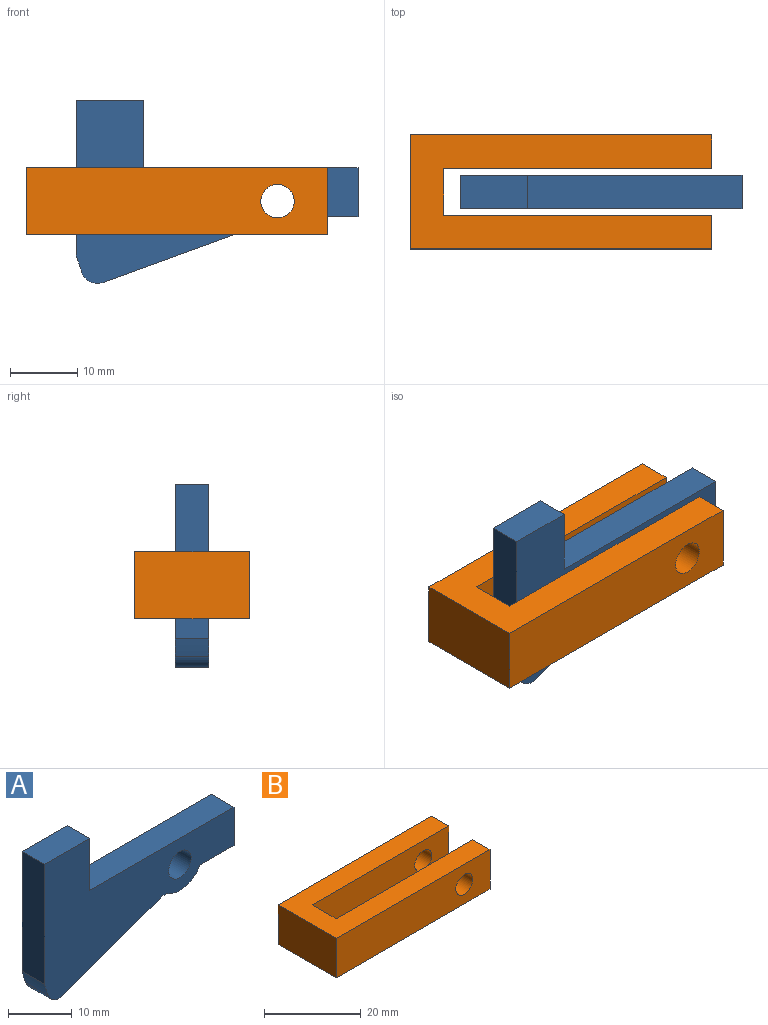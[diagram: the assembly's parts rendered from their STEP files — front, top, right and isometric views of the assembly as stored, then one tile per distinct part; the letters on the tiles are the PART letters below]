
ASSEMBLY  parts=2 mates=1
PART A: 14 faces, bbox 42x5x27.3 mm
  f0: plane 32x5mm, normal (0,0,1), area 160mm2, adj f1,f8,f10,f11
  f1: plane 10x5mm, normal (1,0,0), area 50mm2, adj f0,f2,f10,f11
  f2: plane 10x5mm, normal (0,0,1), area 50mm2, adj f1,f3,f10,f11
  f3: plane 23x5mm, normal (-1,0,0), area 115mm2, adj f2,f4,f10,f11
  f4: cylinder r=31.05mm len=5mm, axis (0,1,0), area 13.7mm2, adj f3,f10,f11,f13
  f5: plane 21.57x7.85mm, normal (0.34,0,-0.94), area 114.8mm2, adj f10,f11,f12,f13
  f6: cylinder r=5mm len=6.78mm, axis (0,1,0), area 39.3mm2, adj f7,f10,f11,f12
  f7: plane 7.59x5mm, normal (0,0,-1), area 37.9mm2, adj f6,f8,f10,f11
  f8: plane 7.35x5mm, normal (1,0,0), area 36.7mm2, adj f0,f7,f10,f11
  f9: cylinder r=2.5mm len=5mm, axis (0,1,0), area 78.5mm2, adj f10,f11
  f10: plane 42x27.26mm, normal (0,-1,0), area 569.3mm2, adj f0,f1,f2,f3,f4,f5,f6,f7
  f11: plane 42x27.26mm, normal (0,1,0), area 569.3mm2, adj f0,f1,f2,f3,f4,f5,f6,f7
  f12: cylinder r=2.5mm len=5mm, axis (0,1,0), area 10.5mm2, adj f5,f6,f10,f11
  f13: cylinder r=2.5mm len=5mm, axis (0,1,0), area 19.6mm2, adj f4,f5,f10,f11
PART B: 12 faces, bbox 45x17x10 mm
  f0: plane 17x10mm, normal (-1,0,0), area 170mm2, adj f1,f7,f8,f9
  f1: plane 45x10mm, normal (0,-1,0), area 430.4mm2, adj f0,f2,f8,f9,f11
  f2: plane 10x5mm, normal (1,0,0), area 50mm2, adj f1,f3,f8,f9
  f3: plane 40x10mm, normal (0,1,0), area 380.4mm2, adj f2,f4,f8,f9,f11
  f4: plane 10x7mm, normal (1,0,0), area 70mm2, adj f3,f5,f8,f9
  f5: plane 40x10mm, normal (0,-1,0), area 380.4mm2, adj f4,f6,f8,f9,f10
  f6: plane 10x5mm, normal (1,0,0), area 50mm2, adj f5,f7,f8,f9
  f7: plane 45x10mm, normal (0,1,0), area 430.4mm2, adj f0,f6,f8,f9,f10
  f8: plane 45x17mm, normal (0,0,1), area 485mm2, adj f0,f1,f2,f3,f4,f5,f6,f7
  f9: plane 45x17mm, normal (0,0,-1), area 485mm2, adj f0,f1,f2,f3,f4,f5,f6,f7
  f10: cylinder r=2.5mm len=5mm, axis (0,-1,0), area 78.5mm2, adj f5,f7
  f11: cylinder r=2.5mm len=5mm, axis (0,-1,0), area 78.5mm2, adj f1,f3
PLACE A rot(axis=(-0.01,-1,0),0deg) t=(43.83,22.04,4.33)mm
PLACE B t=(51.33,19.54,-0.67)mm fixed
MATE revolute B.f10 <-> A.f9  axis (0,-1,0) through (43.83,23.04,4.33)mm
